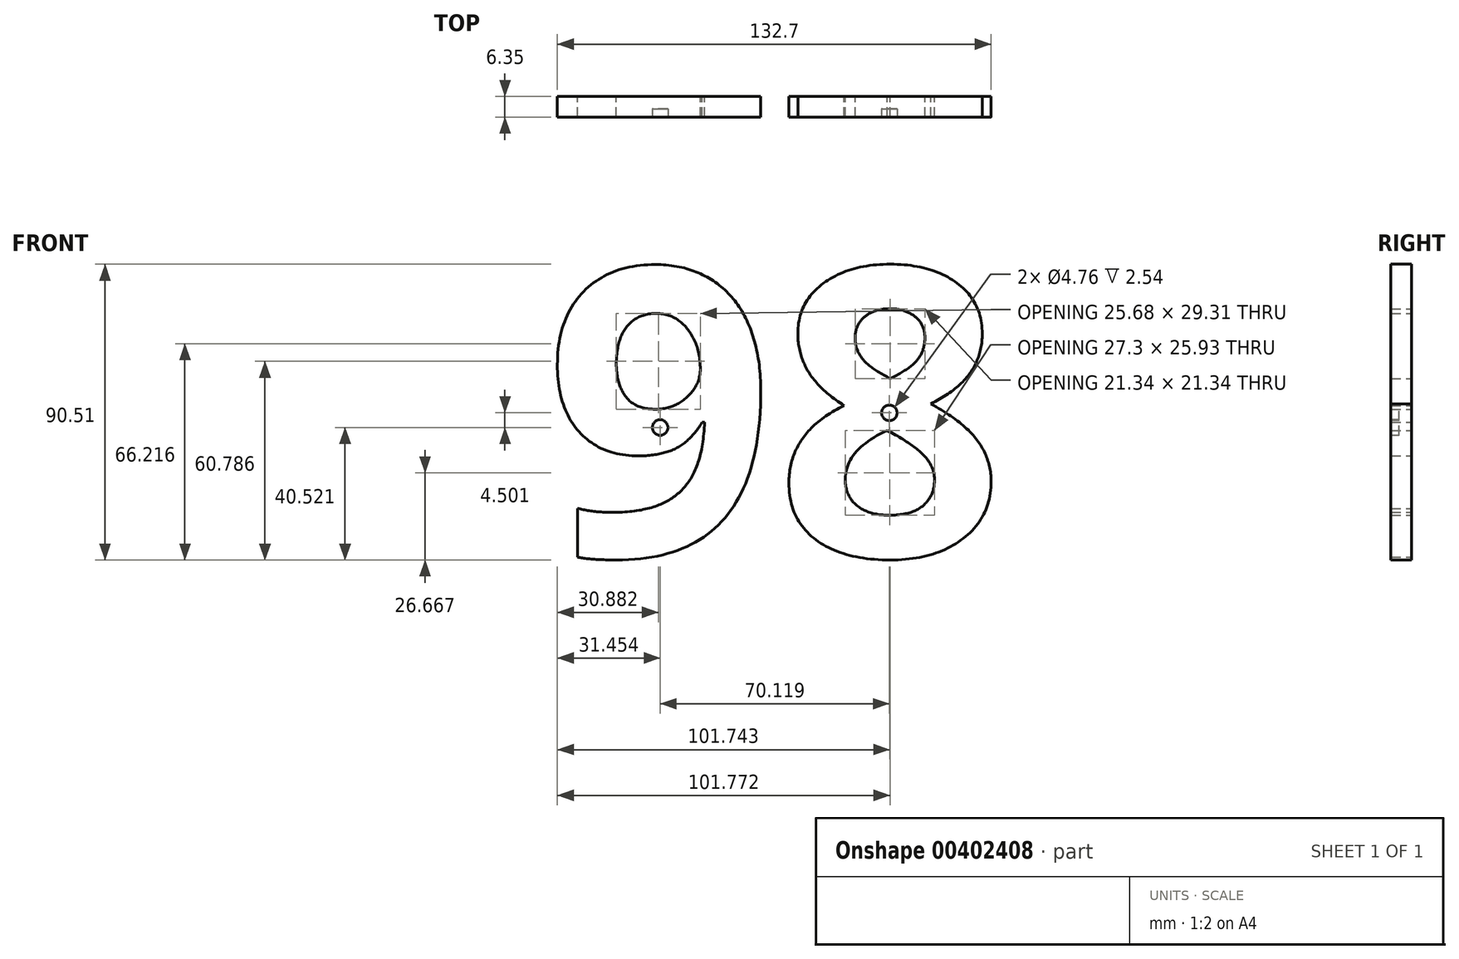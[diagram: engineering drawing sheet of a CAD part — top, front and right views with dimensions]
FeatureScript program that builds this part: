
annotation { "Feature Type Name" : "Feature", "Feature Type Description" : "" }
export const myFeature = defineFeature(function(context is Context, id is Id, definition is map)
    precondition{}
    {
        {
            var Q0;
            Q0=qCreatedBy(makeId("Front.planeOp"),FACE);
            var sketch = newSketch(context, id + "F0", { "sketchPlane" : qUnion([Q0])});
            skText(sketch, "E0", { "text": "98", "fontName": "OpenSans-Bold.ttf"});
            const initialGuessF0  = {"E0": [0, 0, 1, 0, 0.0889]};
            skSetInitialGuess(sketch, initialGuessF0);
            skSolve(sketch);
        }
        {
            var Q0;
            Q0=makeQuery(id+"F0.imprint","IMPRINT",FACE,{"disambiguationData":[TD([[makeQuery(id+"F0.imprint","IMPRINT",EDGE,{"derivedFrom":sQuery(id+"F0.wireOp",EDGE,"E0.sketch_text.stroke-0")}),-1.0]])]});
            var Q1;
            Q1=makeQuery(id+"F0.imprint","IMPRINT",FACE,{"disambiguationData":[TD([[makeQuery(id+"F0.imprint","IMPRINT",EDGE,{"derivedFrom":sQuery(id+"F0.wireOp",EDGE,"E0.sketch_text.stroke-26")}),-1.0]])]});
            var Q2;
            Q2=makeQuery(id+"F0.imprint","IMPRINT",FACE,{"disambiguationData":[TD([[makeQuery(id+"F0.imprint","IMPRINT",EDGE,{"derivedFrom":sQuery(id+"F0.wireOp",EDGE,"E0.sketch_text.stroke-57")}),-1.0]])]});
            var Q3;
            Q3=makeQuery(id+"F0.imprint","IMPRINT",FACE,{"disambiguationData":[TD([[makeQuery(id+"F0.imprint","IMPRINT",EDGE,{"derivedFrom":sQuery(id+"F0.wireOp",EDGE,"E0.sketch_text.stroke-64")}),-1.0]])]});
            var Q4;
            Q4 = qSketchRegion(id + "F2", true);
            extrude(context, id + "F1", {"entities" : qUnion([Q0, Q1, Q2, Q3, Q4]), "depth" : 6.35 * mm, "offsetDistance" : 25.4 * mm});
        }
        {
            var Q0;
            Q0=makeQuery(id+"F1.opExtrude","CAP_FACE",FACE,{"disambiguationData":[OSD([sQuery(id+"F0.wireOp",EDGE,"E0.sketch_text.stroke-0"),sQuery(id+"F0.wireOp",EDGE,"E0.sketch_text.stroke-1"),sQuery(id+"F0.wireOp",EDGE,"E0.sketch_text.stroke-2"),sQuery(id+"F0.wireOp",EDGE,"E0.sketch_text.stroke-3"),sQuery(id+"F0.wireOp",EDGE,"E0.sketch_text.stroke-4"),sQuery(id+"F0.wireOp",EDGE,"E0.sketch_text.stroke-5"),sQuery(id+"F0.wireOp",EDGE,"E0.sketch_text.stroke-6"),sQuery(id+"F0.wireOp",EDGE,"E0.sketch_text.stroke-7"),sQuery(id+"F0.wireOp",EDGE,"E0.sketch_text.stroke-8"),sQuery(id+"F0.wireOp",EDGE,"E0.sketch_text.stroke-9"),sQuery(id+"F0.wireOp",EDGE,"E0.sketch_text.stroke-10"),sQuery(id+"F0.wireOp",EDGE,"E0.sketch_text.stroke-11"),sQuery(id+"F0.wireOp",EDGE,"E0.sketch_text.stroke-12"),sQuery(id+"F0.wireOp",EDGE,"E0.sketch_text.stroke-13"),sQuery(id+"F0.wireOp",EDGE,"E0.sketch_text.stroke-14"),sQuery(id+"F0.wireOp",EDGE,"E0.sketch_text.stroke-15"),sQuery(id+"F0.wireOp",EDGE,"E0.sketch_text.stroke-16"),sQuery(id+"F0.wireOp",EDGE,"E0.sketch_text.stroke-17"),sQuery(id+"F0.wireOp",EDGE,"E0.sketch_text.stroke-18"),sQuery(id+"F0.wireOp",EDGE,"E0.sketch_text.stroke-19"),sQuery(id+"F0.wireOp",EDGE,"E0.sketch_text.stroke-20"),sQuery(id+"F0.wireOp",EDGE,"E0.sketch_text.stroke-21"),sQuery(id+"F0.wireOp",EDGE,"E0.sketch_text.stroke-22"),sQuery(id+"F0.wireOp",EDGE,"E0.sketch_text.stroke-23"),sQuery(id+"F0.wireOp",EDGE,"E0.sketch_text.stroke-24"),sQuery(id+"F0.wireOp",EDGE,"E0.sketch_text.stroke-25")])],"isStart":false});
            var sketch = newSketch(context, id + "F2", { "sketchPlane" : qUnion([Q0])});
            skCircle(sketch, "E1", {"center": v(105.54, 43.8) * mm, "radius": 2.38 * mm});
            skCircle(sketch, "E2", {"center": v(35.42, 39.3) * mm, "radius": 2.38 * mm});
            skSolve(sketch);
        }
        {
            var Q0;
            Q0 = qSketchRegion(id + "F2", true);
            var Q1;
            Q1=sQuery(id+"F2.wireOp",EDGE,"E1");
            extrude(context, id + "F3", {"entities" : qUnion([Q0]), "operationType" : NewBodyOperationType.REMOVE, "surfaceEntities" : qUnion([Q1]), "oppositeDirection" : true, "depth" : 2.54 * mm, "offsetDistance" : 25.4 * mm});
        }
    });
